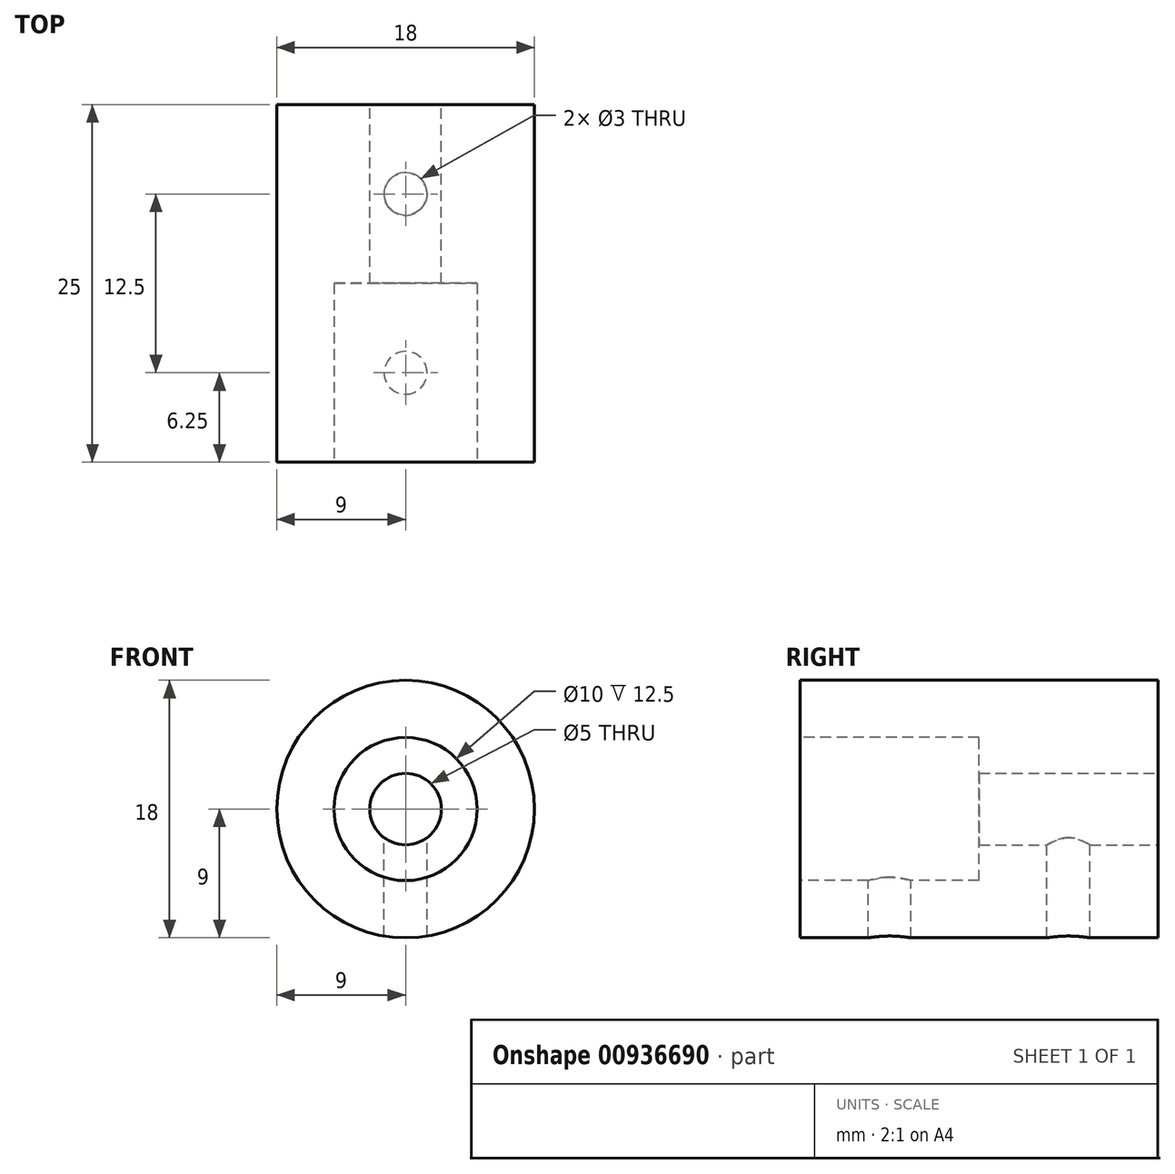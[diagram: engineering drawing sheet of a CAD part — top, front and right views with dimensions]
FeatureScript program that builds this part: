
annotation { "Feature Type Name" : "Feature", "Feature Type Description" : "" }
export const myFeature = defineFeature(function(context is Context, id is Id, definition is map)
    precondition{}
    {
        {
            var Q0;
            Q0=qCreatedBy(makeId("Front.planeOp"),FACE);
            var sketch = newSketch(context, id + "F0", { "sketchPlane" : qUnion([Q0])});
            skCircle(sketch, "E0", {"center": v(0, 0) * mm, "radius": 9 * mm});
            skSolve(sketch);
        }
        {
            var Q0;
            Q0=makeQuery(id+"F0.imprint","IMPRINT",FACE,{"disambiguationData":[TD([[makeQuery(id+"F0.imprint","IMPRINT",EDGE,{"derivedFrom":sQuery(id+"F0.wireOp",EDGE,"E0")}),1.0]])]});
            extrude(context, id + "F1", {"entities" : qUnion([Q0]), "depth" : 25 * mm, "offsetDistance" : 25 * mm});
        }
        {
            var Q0;
            Q0=makeQuery(id+"F1.opExtrude","CAP_FACE",FACE,{"disambiguationData":[OSD([sQuery(id+"F0.wireOp",EDGE,"E0")])],"isStart":false});
            var sketch = newSketch(context, id + "F2", { "sketchPlane" : qUnion([Q0])});
            skCircle(sketch, "E1", {"center": v(0, 0) * mm, "radius": 5 * mm});
            skSolve(sketch);
        }
        {
            var Q0;
            Q0=makeQuery(id+"F2.imprint","IMPRINT",FACE,{"disambiguationData":[TD([[makeQuery(id+"F2.imprint","IMPRINT",EDGE,{"derivedFrom":sQuery(id+"F2.wireOp",EDGE,"E1")}),1.0]])]});
            extrude(context, id + "F3", {"entities" : qUnion([Q0]), "operationType" : NewBodyOperationType.REMOVE, "oppositeDirection" : true, "depth" : 12.5 * mm, "offsetDistance" : 25 * mm});
        }
        {
            var Q0;
            Q0=makeQuery(id+"F1.opExtrude","CAP_FACE",FACE,{"disambiguationData":[OSD([sQuery(id+"F0.wireOp",EDGE,"E0")])],"isStart":true});
            var sketch = newSketch(context, id + "F4", { "sketchPlane" : qUnion([Q0])});
            skCircle(sketch, "E2", {"center": v(0, 0) * mm, "radius": 2.5 * mm});
            skSolve(sketch);
        }
        {
            var Q0;
            Q0=makeQuery(id+"F4.imprint","IMPRINT",FACE,{"disambiguationData":[TD([[makeQuery(id+"F4.imprint","IMPRINT",EDGE,{"derivedFrom":sQuery(id+"F4.wireOp",EDGE,"E2")}),1.0]])]});
            extrude(context, id + "F5", {"entities" : qUnion([Q0]), "operationType" : NewBodyOperationType.REMOVE, "oppositeDirection" : true, "depth" : 12.5 * mm, "offsetDistance" : 25 * mm});
        }
        {
            var Q0;
            Q0=qCreatedBy(makeId("Top.planeOp"),FACE);
            var sketch = newSketch(context, id + "F6", { "sketchPlane" : qUnion([Q0])});
            skCircle(sketch, "E3", {"center": v(0, -6.25) * mm, "radius": 1.5 * mm});
            skCircle(sketch, "E4", {"center": v(0, -18.75) * mm, "radius": 1.5 * mm});
            skSolve(sketch);
        }
        {
            var Q0;
            Q0=makeQuery(id+"F6.imprint","IMPRINT",FACE,{"disambiguationData":[TD([[makeQuery(id+"F6.imprint","IMPRINT",EDGE,{"derivedFrom":sQuery(id+"F6.wireOp",EDGE,"E3")}),1.0]])]});
            var Q1;
            Q1=makeQuery(id+"F6.imprint","IMPRINT",FACE,{"disambiguationData":[TD([[makeQuery(id+"F6.imprint","IMPRINT",EDGE,{"derivedFrom":sQuery(id+"F6.wireOp",EDGE,"E4")}),1.0]])]});
            extrude(context, id + "F7", {"entities" : qUnion([Q0, Q1]), "operationType" : NewBodyOperationType.REMOVE, "oppositeDirection" : true, "depth" : 25 * mm, "offsetDistance" : 25 * mm});
        }
    });
